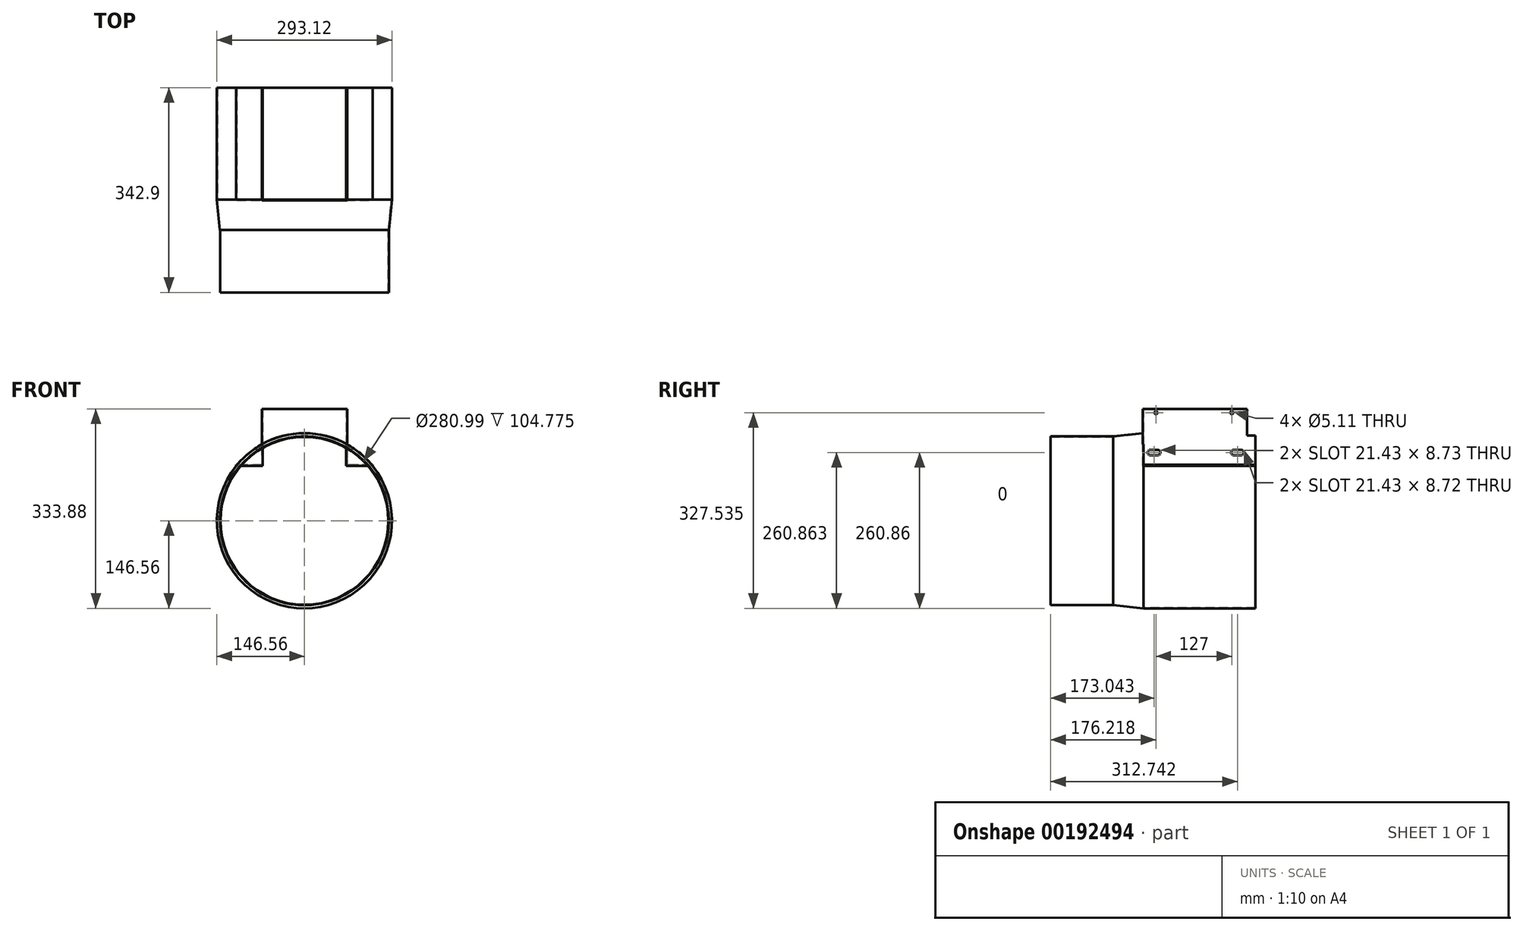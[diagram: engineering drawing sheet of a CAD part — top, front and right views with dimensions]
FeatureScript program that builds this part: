
annotation { "Feature Type Name" : "Feature", "Feature Type Description" : "" }
export const myFeature = defineFeature(function(context is Context, id is Id, definition is map)
    precondition{}
    {
        {
            var Q0;
            Q0=qCreatedBy(makeId("Front.planeOp"),FACE);
            var sketch = newSketch(context, id + "F0", { "sketchPlane" : qUnion([Q0])});
            skCircle(sketch, "E0", {"center": v(0, 0) * mm, "radius": 140.5 * mm});
            skCircle(sketch, "E1", {"center": v(0, 0) * mm, "radius": 141.29 * mm});
            skCircle(sketch, "E2", {"center": v(0, 0) * mm, "radius": 146.56 * mm, "construction": true});
            skSolve(sketch);
        }
        {
            var Q0;
            Q0=makeQuery(id+"F0.imprint","IMPRINT",FACE,{"disambiguationData":[TD([[makeQuery(id+"F0.imprint","IMPRINT",EDGE,{"derivedFrom":sQuery(id+"F0.wireOp",EDGE,"E0")}),-1.0]])]});
            extrude(context, id + "F1", {"entities" : qUnion([Q0]), "depth" : 104.77 * mm});
        }
        {
            var Q0;
            Q0=qCreatedBy(makeId("Front.planeOp"),FACE);
            var sketch = newSketch(context, id + "F2", { "sketchPlane" : qUnion([Q0])});
            skLineSegment(sketch, "E3", {"start": v(0, 0) * mm, "end": v(0, 168.95) * mm, "construction": true});
            skSolve(sketch);
        }
        {
            var Q0;
            Q0=qCreatedBy(makeId("Right.planeOp"),FACE);
            var sketch = newSketch(context, id + "F3", { "sketchPlane" : qUnion([Q0])});
            skLineSegment(sketch, "E4", {"start": v(0, 140.5) * mm, "end": v(0, 141.35) * mm});
            skLineSegment(sketch, "E5", {"start": v(0, 141.35) * mm, "end": v(50.8, 146.56) * mm});
            skLineSegment(sketch, "E6", {"start": v(0, 140.5) * mm, "end": v(50.8, 145.72) * mm});
            skLineSegment(sketch, "E7", {"start": v(50.8, 146.56) * mm, "end": v(50.8, 145.72) * mm});
            skLineSegment(sketch, "E8", {"start": v(0, 0) * mm, "end": v(87.13, 0) * mm, "construction": true});
            skSolve(sketch);
        }
        {
            var Q0;
            Q0 = qSketchRegion(id + "F3", true);
            var Q1;
            Q1=sQuery(id+"F3.wireOp",EDGE,"E8");
            revolve(context, id + "F4", {"operationType" : NewBodyOperationType.ADD, "entities" : qUnion([Q0]), "axis" : qUnion([Q1]), "revolveType" : RevolveType.FULL});
        }
        {
            var Q0;
            Q0=qCreatedBy(makeId("Top.planeOp"),FACE);
            cPlane(context, id + "F5", {"entities" : qUnion([Q0]), "cplaneType" : CPlaneType.OFFSET, "offset" : 92.07 * mm, "width" : 152.4 * mm, "height" : 152.4 * mm});
        }
        {
            var Q0;
            Q0=makeQuery(id+"F4.opRevolve","SWEPT_FACE",FACE,{"disambiguationData":[OSD([sQuery(id+"F3.wireOp",EDGE,"E7")])]});
            var sketch = newSketch(context, id + "F6", { "sketchPlane" : qUnion([Q0])});
            skCircle(sketch, "E9.0", {"center": v(0, 0) * mm, "radius": 146.56 * mm});
            skCircle(sketch, "E10.0", {"center": v(0, 0) * mm, "radius": 145.72 * mm});
            skSolve(sketch);
        }
        {
            var Q0;
            Q0 = qSketchRegion(id + "F6", true);
            extrude(context, id + "F7", {"entities" : qUnion([Q0]), "operationType" : NewBodyOperationType.ADD, "depth" : 187.32 * mm});
        }
        {
            var Q0;
            Q0=qCreatedBy(id+"F5.planeOp",FACE);
            var sketch = newSketch(context, id + "F8", { "sketchPlane" : qUnion([Q0])});
            skLineSegment(sketch, "E11.bottom", {"start": v(177.8, 50.8) * mm, "end": v(-177.8, 50.8) * mm});
            skLineSegment(sketch, "E11.top", {"start": v(177.8, 238.13) * mm, "end": v(-177.8, 238.12) * mm});
            skLineSegment(sketch, "E11.left", {"start": v(177.8, 50.8) * mm, "end": v(177.8, 238.13) * mm});
            skLineSegment(sketch, "E11.right", {"start": v(-177.8, 50.8) * mm, "end": v(-177.8, 238.12) * mm});
            skSolve(sketch);
        }
        {
            var Q0;
            Q0 = qSketchRegion(id + "F8", true);
            extrude(context, id + "F9", {"entities" : qUnion([Q0]), "operationType" : NewBodyOperationType.REMOVE, "endBound" : BoundingType.THROUGH_ALL, "depth" : 25.4 * mm});
        }
        {
            var Q0;
            Q0=qCreatedBy(id+"F5.planeOp",FACE);
            var sketch = newSketch(context, id + "F10", { "sketchPlane" : qUnion([Q0])});
            skLineSegment(sketch, "E12.0", {"start": v(114.02, 238.13) * mm, "end": v(114.02, 50.8) * mm});
            skLineSegment(sketch, "E13.0", {"start": v(-114.02, 50.8) * mm, "end": v(-114.02, 238.13) * mm});
            skLineSegment(sketch, "E14.0", {"start": v(114.02, 50.8) * mm, "end": v(69.85, 50.8) * mm});
            skLineSegment(sketch, "E15", {"start": v(69.85, 50.8) * mm, "end": v(69.85, 238.13) * mm});
            skLineSegment(sketch, "E16", {"start": v(114.02, 238.13) * mm, "end": v(69.85, 238.13) * mm});
            skLineSegment(sketch, "E17", {"start": v(-69.85, 50.8) * mm, "end": v(-69.85, 238.12) * mm});
            skLineSegment(sketch, "E18", {"start": v(-114.02, 238.13) * mm, "end": v(-69.85, 238.13) * mm});
            skLineSegment(sketch, "E19.trimOffspring", {"start": v(-69.85, 50.8) * mm, "end": v(-114.02, 50.8) * mm});
            skSolve(sketch);
        }
        {
            var Q0;
            Q0 = qSketchRegion(id + "F10", true);
            extrude(context, id + "F11", {"entities" : qUnion([Q0]), "operationType" : NewBodyOperationType.ADD, "depth" : 1.59 * mm});
        }
        {
            var Q0;
            Q0=makeQuery(id+"F11.opExtrude","CAP_FACE",FACE,{"disambiguationData":[OSD([sQuery(id+"F10.wireOp",EDGE,"E12.0"),sQuery(id+"F10.wireOp",EDGE,"E14.0"),sQuery(id+"F10.wireOp",EDGE,"E15"),sQuery(id+"F10.wireOp",EDGE,"E16")])],"isStart":false});
            var sketch = newSketch(context, id + "F12", { "sketchPlane" : qUnion([Q0])});
            skLineSegment(sketch, "E20.0", {"start": v(69.85, 50.8) * mm, "end": v(69.85, 238.13) * mm});
            skLineSegment(sketch, "E21.0", {"start": v(71.44, 50.8) * mm, "end": v(71.44, 238.13) * mm});
            skLineSegment(sketch, "E22", {"start": v(71.44, 238.13) * mm, "end": v(69.85, 238.13) * mm});
            skLineSegment(sketch, "E23", {"start": v(71.44, 50.8) * mm, "end": v(69.85, 50.8) * mm});
            skLineSegment(sketch, "E24.0", {"start": v(-69.85, 50.8) * mm, "end": v(-69.85, 238.13) * mm});
            skLineSegment(sketch, "E25.0", {"start": v(-71.44, 50.8) * mm, "end": v(-71.44, 238.13) * mm});
            skLineSegment(sketch, "E26", {"start": v(-69.85, 238.13) * mm, "end": v(-71.44, 238.13) * mm});
            skLineSegment(sketch, "E27", {"start": v(-69.85, 50.8) * mm, "end": v(-71.44, 50.8) * mm});
            skSolve(sketch);
        }
        {
            var Q0;
            Q0 = qSketchRegion(id + "F12", true);
            extrude(context, id + "F13", {"entities" : qUnion([Q0]), "operationType" : NewBodyOperationType.ADD, "depth" : 93.66 * mm});
        }
        {
            var Q0;
            Q0=makeQuery(id+"F13.boolean.opBoolean","SPLIT",FACE,{"disambiguationData":[TD([makeQuery(id+"F13.opExtrude","SWEPT_FACE",FACE,{"disambiguationData":[OSD([sQuery(id+"F12.wireOp",EDGE,"E21.0")])]})])],"derivedFrom":makeQuery(id+"F9.boolean.opBoolean","COPY",FACE,{"derivedFrom":makeQuery(id+"F9.opExtrude","SWEPT_FACE",FACE,{"disambiguationData":[OSD([sQuery(id+"F8.wireOp",EDGE,"E11.bottom")])]})})});
            var sketch = newSketch(context, id + "F14", { "sketchPlane" : qUnion([Q0])});
            skArc(sketch, "E28", {"start": v(112.6, 92.07) * mm, "mid": v(92.94, 111.89) * mm, "end": v(69.85, 127.58) * mm});
            skLineSegment(sketch, "E29.0", {"start": v(-112.94, 92.08) * mm, "end": v(-112.6, 92.08) * mm});
            skLineSegment(sketch, "E30.0", {"start": v(112.94, 92.08) * mm, "end": v(69.85, 92.08) * mm});
            skPoint(sketch, "E31.orphan", {"position": v(-69.85, 92.08) * mm});
            skLineSegment(sketch, "E32", {"start": v(-112.6, 92.08) * mm, "end": v(-69.85, 92.08) * mm});
            skLineSegment(sketch, "E33.0", {"start": v(-69.85, 187.32) * mm, "end": v(-69.85, 92.08) * mm});
            skLineSegment(sketch, "E34.0", {"start": v(69.85, 187.32) * mm, "end": v(69.85, 92.08) * mm});
            skLineSegment(sketch, "E35.trimOffspring", {"start": v(69.85, 92.08) * mm, "end": v(112.94, 92.08) * mm});
            skArc(sketch, "E36.trimOffspring", {"start": v(-69.85, 127.58) * mm, "mid": v(-92.94, 111.89) * mm, "end": v(-112.6, 92.08) * mm});
            skSolve(sketch);
        }
        {
            var Q0;
            Q0 = qSketchRegion(id + "F14", true);
            extrude(context, id + "F15", {"entities" : qUnion([Q0]), "operationType" : NewBodyOperationType.ADD, "oppositeDirection" : true, "depth" : 1.59 * mm});
        }
        {
            var Q0;
            {var subQ0=sQuery(id+"F10.wireOp",EDGE,"E15");var subQ4=sQuery(id+"F14.wireOp",EDGE,"E32");var subQ5=sQuery(id+"F14.wireOp",EDGE,"E28");Q0=makeQuery(id+"F15.boolean.opBoolean","SPLIT",FACE,{"disambiguationData":[TD([makeQuery(id+"F11.opExtrude","SWEPT_FACE",FACE,{"disambiguationData":[OSD([subQ0])]})])],"derivedFrom":makeQuery(id+"F15.opExtrude","CAP_FACE",FACE,{"disambiguationData":[OSD([subQ5,subQ4])],"isStart":true})});}
            var sketch = newSketch(context, id + "F16", { "sketchPlane" : qUnion([Q0])});
            skArc(sketch, "E37", {"start": v(71.44, 128) * mm, "mid": v(0, 146.6) * mm, "end": v(-71.44, 128) * mm});
            skLineSegment(sketch, "E38.0", {"start": v(-71.44, 187.33) * mm, "end": v(-71.44, 128) * mm});
            skLineSegment(sketch, "E39.0", {"start": v(71.44, 187.33) * mm, "end": v(71.44, 128) * mm});
            skLineSegment(sketch, "E40", {"start": v(-71.44, 187.33) * mm, "end": v(71.44, 187.33) * mm});
            skPoint(sketch, "E41.orphan", {"position": v(-71.44, 93.66) * mm});
            skPoint(sketch, "E42.orphan", {"position": v(71.44, 93.66) * mm});
            skSolve(sketch);
        }
        {
            var Q0;
            Q0 = qSketchRegion(id + "F16", true);
            extrude(context, id + "F17", {"entities" : qUnion([Q0]), "operationType" : NewBodyOperationType.ADD, "oppositeDirection" : true, "depth" : 1.59 * mm});
        }
        {
            var Q0;
            Q0=makeQuery(id+"F17.boolean.opBoolean","MERGE",FACE,{"derivedFrom":[makeQuery(id+"F13.opExtrude","SWEPT_FACE",FACE,{"disambiguationData":[OSD([sQuery(id+"F12.wireOp",EDGE,"E25.0")])]}),makeQuery(id+"F17.opExtrude","SWEPT_FACE",FACE,{"disambiguationData":[OSD([sQuery(id+"F16.wireOp",EDGE,"E39.0")])]})]});
            var sketch = newSketch(context, id + "F18", { "sketchPlane" : qUnion([Q0])});
            skLineSegment(sketch, "E43.bottom", {"start": v(-238.13, 187.33) * mm, "end": v(-223.84, 187.33) * mm});
            skLineSegment(sketch, "E43.top", {"start": v(-238.13, 142.88) * mm, "end": v(-223.84, 142.88) * mm});
            skLineSegment(sketch, "E43.left", {"start": v(-238.13, 187.33) * mm, "end": v(-238.13, 142.88) * mm});
            skLineSegment(sketch, "E43.right", {"start": v(-223.84, 187.32) * mm, "end": v(-223.84, 142.87) * mm});
            skSolve(sketch);
        }
        {
            var Q0;
            Q0 = qSketchRegion(id + "F18", true);
            extrude(context, id + "F19", {"entities" : qUnion([Q0]), "operationType" : NewBodyOperationType.REMOVE, "endBound" : BoundingType.THROUGH_ALL, "oppositeDirection" : true, "depth" : 25.4 * mm});
        }
        {
            var Q0;
            Q0=makeQuery(id+"F17.boolean.opBoolean","MERGE",FACE,{"derivedFrom":[makeQuery(id+"F13.opExtrude","SWEPT_FACE",FACE,{"disambiguationData":[OSD([sQuery(id+"F12.wireOp",EDGE,"E25.0")])]}),makeQuery(id+"F17.opExtrude","SWEPT_FACE",FACE,{"disambiguationData":[OSD([sQuery(id+"F16.wireOp",EDGE,"E39.0")])]})]});
            var sketch = newSketch(context, id + "F20", { "sketchPlane" : qUnion([Q0])});
            skArc(sketch, "E44", {"start": v(-62.04, 109.94) * mm, "mid": v(-57.55, 114.26) * mm, "end": v(-61.95, 118.67) * mm});
            skArc(sketch, "E45", {"start": v(-201.85, 109.94) * mm, "mid": v(-197.25, 114.19) * mm, "end": v(-201.63, 118.67) * mm});
            skArc(sketch, "E46.1.0.0", {"start": v(-74.61, 118.67) * mm, "mid": v(-78.98, 114.3) * mm, "end": v(-74.61, 109.93) * mm});
            skLineSegment(sketch, "E46.direction1", {"start": v(-61.91, 114.3) * mm, "end": v(-74.61, 114.3) * mm, "construction": true});
            skLineSegment(sketch, "E47", {"start": v(-61.87, 118.67) * mm, "end": v(-74.61, 118.67) * mm});
            skLineSegment(sketch, "E48", {"start": v(-61.79, 109.94) * mm, "end": v(-74.61, 109.93) * mm});
            skArc(sketch, "E49.1.0.0", {"start": v(-214.31, 118.67) * mm, "mid": v(-218.68, 114.18) * mm, "end": v(-214.07, 109.94) * mm});
            skLineSegment(sketch, "E49.direction1", {"start": v(-201.61, 114.3) * mm, "end": v(-214.31, 114.3) * mm, "construction": true});
            skLineSegment(sketch, "E50", {"start": v(-201.63, 118.67) * mm, "end": v(-214.31, 118.67) * mm});
            skLineSegment(sketch, "E51", {"start": v(-201.85, 109.94) * mm, "end": v(-214.55, 109.94) * mm});
            skCircle(sketch, "E52", {"center": v(-71.44, 180.98) * mm, "radius": 2.55 * mm});
            skCircle(sketch, "E53.1.0.0", {"center": v(-198.44, 180.98) * mm, "radius": 2.55 * mm});
            skLineSegment(sketch, "E53.direction1", {"start": v(-71.44, 180.98) * mm, "end": v(-198.44, 180.98) * mm, "construction": true});
            skSolve(sketch);
        }
        {
            var Q0;
            Q0 = qSketchRegion(id + "F20", true);
            extrude(context, id + "F21", {"entities" : qUnion([Q0]), "operationType" : NewBodyOperationType.REMOVE, "endBound" : BoundingType.THROUGH_ALL, "oppositeDirection" : true, "depth" : 25.4 * mm});
        }
    });
